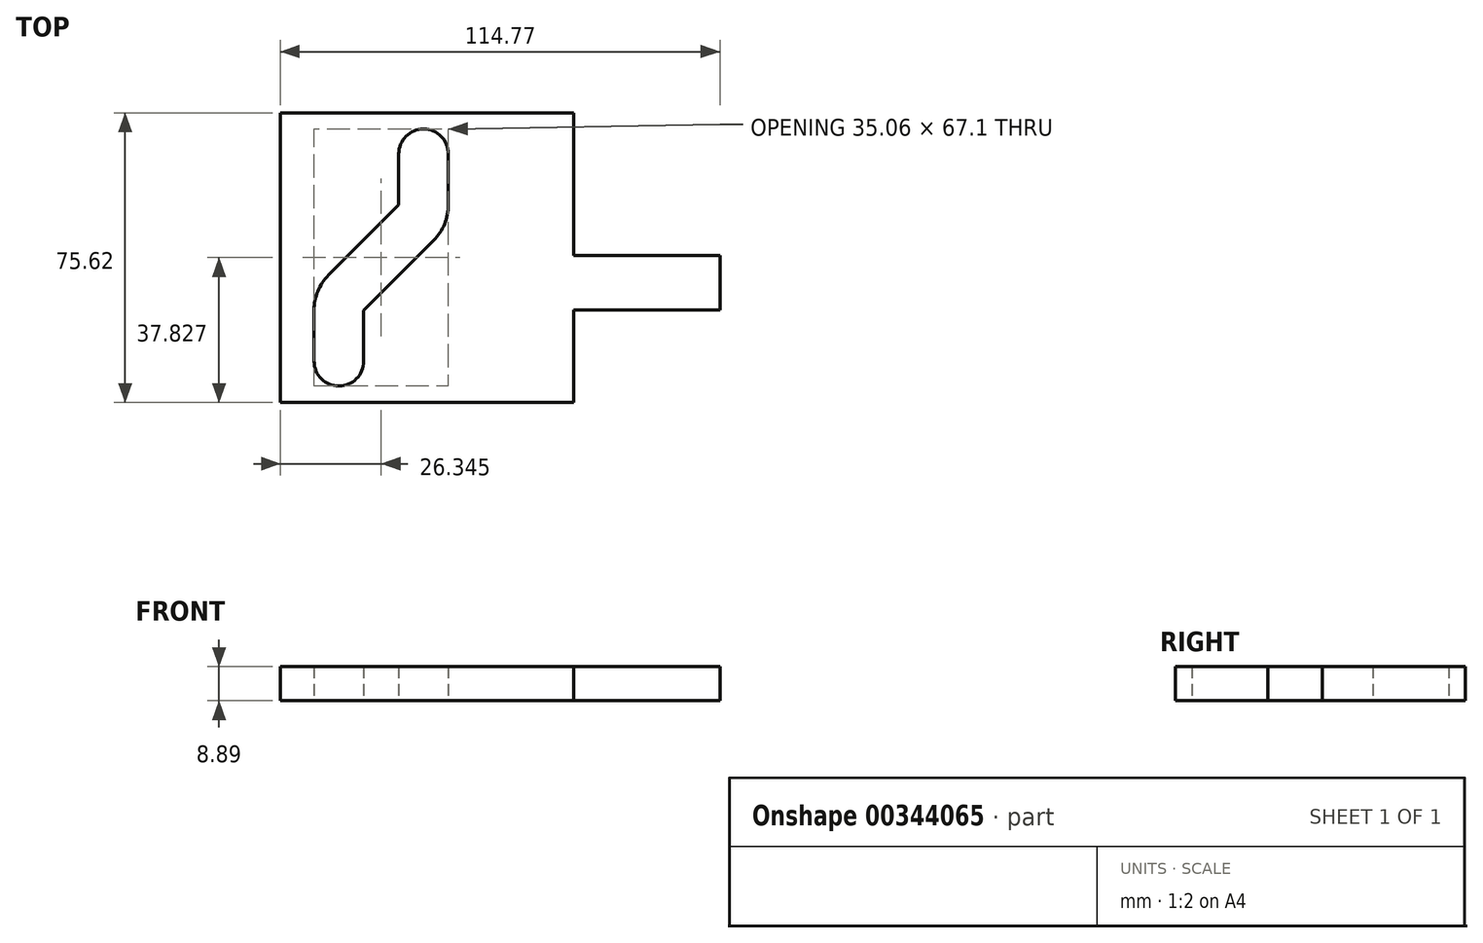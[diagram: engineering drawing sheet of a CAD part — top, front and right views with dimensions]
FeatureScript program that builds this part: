
annotation { "Feature Type Name" : "Feature", "Feature Type Description" : "" }
export const myFeature = defineFeature(function(context is Context, id is Id, definition is map)
    precondition{}
    {
        {
            var Q0;
            Q0=qCreatedBy(makeId("Top.planeOp"),FACE);
            var sketch = newSketch(context, id + "F0", { "sketchPlane" : qUnion([Q0])});
            skLineSegment(sketch, "E0", {"start": v(-130, -28.3) * mm, "end": v(-130, 22.5) * mm});
            skLineSegment(sketch, "E1", {"start": v(-135.62, -22.69) * mm, "end": v(-126.46, -13.53) * mm});
            skLineSegment(sketch, "E2.MirrorCS", {"start": v(-135.62, -22.69) * mm, "end": v(-144.78, -31.85) * mm});
            skLineSegment(sketch, "E3.MirrorCS", {"start": v(-126.45, -31.84) * mm, "end": v(-135.61, -41) * mm});
            skLineSegment(sketch, "E4", {"start": v(-135.62, -22.69) * mm, "end": v(-144.77, -31.84) * mm});
            skLineSegment(sketch, "E5", {"start": v(-126.45, -31.84) * mm, "end": v(-117.3, -22.69) * mm});
            skPoint(sketch, "E6.visualSharp", {"position": v(-113.5, -18.9) * mm});
            skArc(sketch, "E6.filletArc", {"start": v(-117.3, -22.69) * mm, "mid": v(-114.49, -18.49) * mm, "end": v(-113.5, -13.53) * mm});
            skPoint(sketch, "E7.visualSharp", {"position": v(-148.57, -35.64) * mm});
            skArc(sketch, "E7.filletArc", {"start": v(-144.77, -31.84) * mm, "mid": v(-147.58, -36.05) * mm, "end": v(-148.57, -41) * mm});
            skPoint(sketch, "E8.first.point", {"position": v(-135.61, -55.07) * mm});
            skPoint(sketch, "E8.second.point", {"position": v(-148.57, -54.3) * mm});
            skLineSegment(sketch, "E9", {"start": v(-135.61, -41) * mm, "end": v(-135.61, -54.3) * mm});
            skArc(sketch, "E10", {"start": v(-148.57, -54.3) * mm, "mid": v(-142.09, -60.78) * mm, "end": v(-135.61, -54.3) * mm});
            skLineSegment(sketch, "E11", {"start": v(-148.57, -41) * mm, "end": v(-148.57, -54.3) * mm});
            skLineSegment(sketch, "E12", {"start": v(-113.5, -13.53) * mm, "end": v(-113.5, -0.16) * mm});
            skLineSegment(sketch, "E13", {"start": v(-126.46, -13.53) * mm, "end": v(-126.46, -0.16) * mm});
            skArc(sketch, "E14", {"start": v(-113.5, -0.16) * mm, "mid": v(-119.98, 6.32) * mm, "end": v(-126.46, -0.16) * mm});
            skLineSegment(sketch, "E15.right", {"start": v(-157.38, -26.38) * mm, "end": v(-157.38, 10.56) * mm});
            skPoint(sketch, "E16.endSnap0", {"position": v(-142.09, -60.78) * mm});
            skLineSegment(sketch, "E17", {"start": v(-157.38, -26.38) * mm, "end": v(-157.38, -65.06) * mm});
            skLineSegment(sketch, "E18", {"start": v(-42.6, -33.84) * mm, "end": v(-42.6, -26.73) * mm});
            skLineSegment(sketch, "E19.MirrorCS", {"start": v(-42.6, -33.84) * mm, "end": v(-42.6, -40.96) * mm});
            skLineSegment(sketch, "E20", {"start": v(-42.6, -26.73) * mm, "end": v(-80.72, -26.73) * mm});
            skLineSegment(sketch, "E21.MirrorCS", {"start": v(-42.6, -40.96) * mm, "end": v(-80.72, -40.96) * mm});
            skLineSegment(sketch, "E22", {"start": v(-80.72, -26.73) * mm, "end": v(-80.72, 10.56) * mm});
            skLineSegment(sketch, "E23", {"start": v(-80.72, -40.96) * mm, "end": v(-80.72, -65.06) * mm});
            skLineSegment(sketch, "E24", {"start": v(-157.38, 10.56) * mm, "end": v(-80.72, 10.56) * mm});
            skLineSegment(sketch, "E25", {"start": v(-157.38, -65.06) * mm, "end": v(-80.72, -65.06) * mm});
            skSolve(sketch);
        }
        {
            var Q0;
            Q0 = qSketchRegion(id + "F0", true);
            extrude(context, id + "F1", {"entities" : qUnion([Q0]), "depth" : 8.9 * mm});
        }
    });
